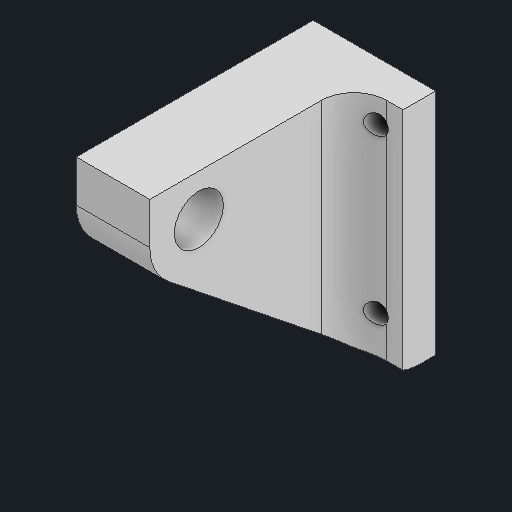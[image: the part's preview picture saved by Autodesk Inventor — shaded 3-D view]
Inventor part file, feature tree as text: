
AUTODESK INVENTOR PART (.ipt)
format: ipt  version: 2025 (Build 290162000, 162)  size: 166,912 bytes
history: native  units: mm
features: extrude x4, sketch x4, fillet x2, reference x2, other x2
ambient origin geometry x8: Origin, YZ Plane, XZ Plane, XY Plane, X Axis, Y Axis, Z Axis, Center Point
bodies: 实体1 (feature_tree)
feature tree (14):
  extrude  "拉伸1"  Depth=4.0mm
  extrude  "拉伸2"  Depth=25.0mm TaperAngle=0.0deg
  extrude  "拉伸3"  Depth=25.0mm TaperAngle=0.0deg
  fillet  "圆角1"  Radius=6.0mm
  extrude  "拉伸4"  Depth=4.0mm TaperAngle=0.0deg
  fillet  "圆角2"  Radius=4.0mm
  sketch  "草图1"  dims[d1=4.0mm d2=0.0mm d3=15.0mm]
  reference  "参考1"
  sketch  "草图2"  dims[d4=28.0mm d5=25.0mm d6=0.0mm]
  reference  "参考2"
  sketch  "草图3"  dims[d7=20.0mm d8=25.0mm d9=0.0mm d10=6.0mm]
  sketch  "草图4"  dims[d11=6.0mm d12=25.0mm d13=0.0mm d14=4.0mm]
  other  "南京理工大学AllianceV3全向轮组装配(1).iam"
  other  "南京理工大学Alliance转接件-4孔_41"
